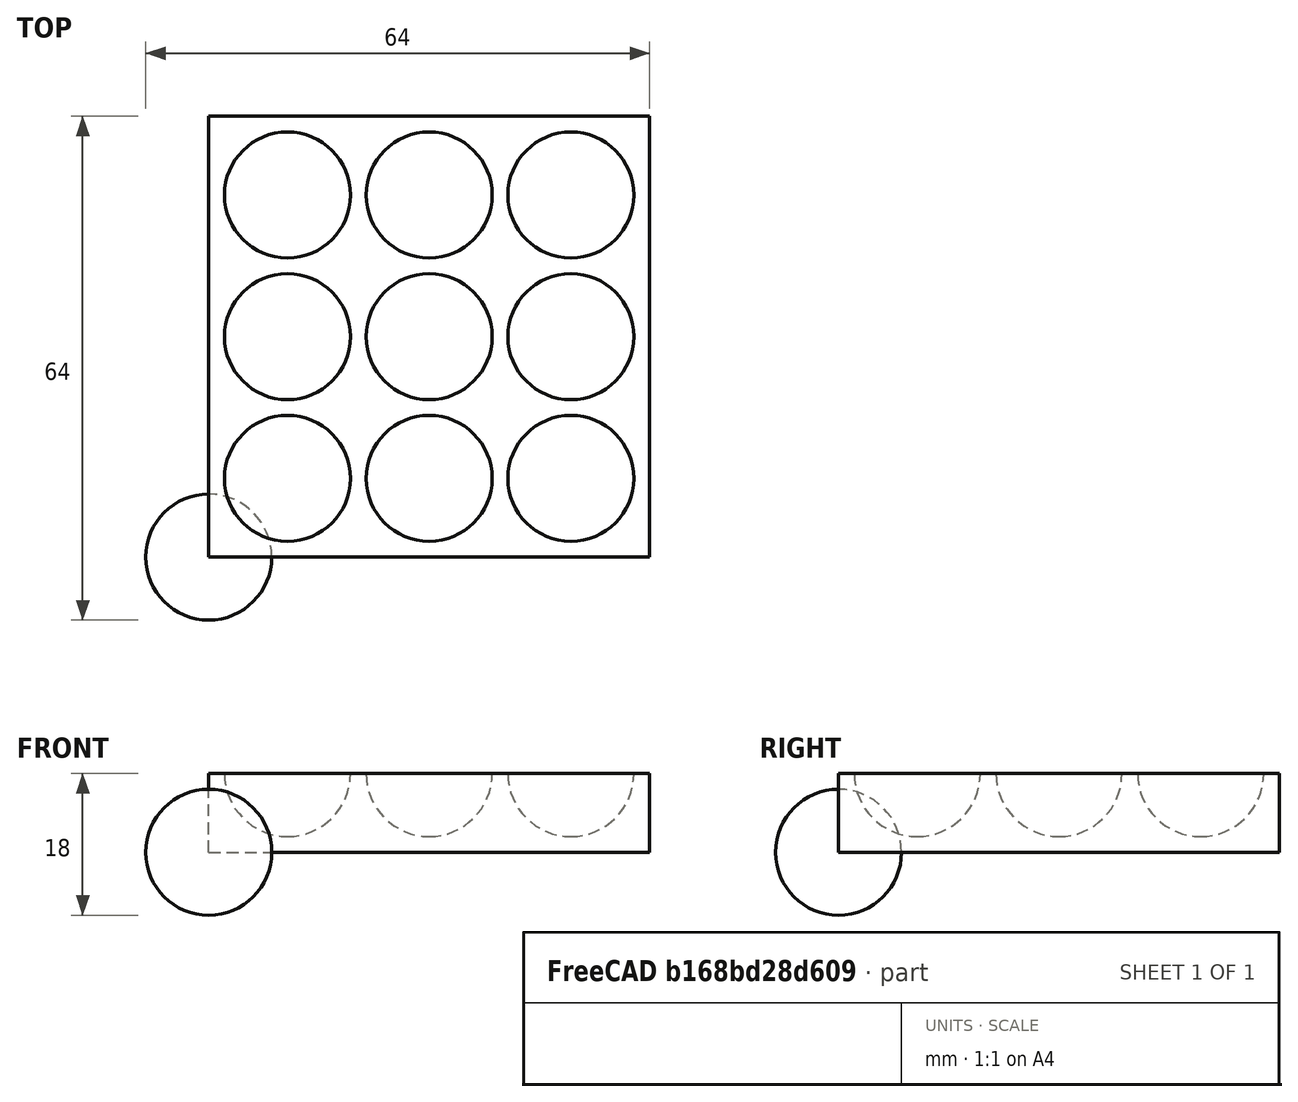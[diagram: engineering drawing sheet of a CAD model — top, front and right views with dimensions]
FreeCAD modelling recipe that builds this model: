
FCSTD DOCUMENT  (FreeCAD 1.0R39319 (Git))
Label: ojt1_t13p01_spheres
License: All rights reserved
LicenseURL: https://en.wikipedia.org/wiki/All_rights_reserved
objects: Part::Sphere×1, Part::FeaturePython×1, Part::Box×1, Part::Cut×1
note: 3 computed .brp shape members not serialized (recipe doc carries the construction recipe); baked Part::Feature solids carry a one-line shape summary decoded from their .brp

FEATURE [Part::Sphere] Sphere  label="Esfera"
  Angle1 = -90
  Angle2 = 90
  Angle3 = 360
  AttacherType = Attacher::AttachEngine3D
  Radius = 8
FEATURE [Part::FeaturePython] Array  # Draft array (typed FeaturePython)
  AlwaysSyncPlacement = false
  Angle = 360
  ArrayType = 0
  Axis = (0,0,1)
  Base = -> Sphere
  Center = (0,0,0)
  Count = 9
  ExpandArray = false
  Fuse = false
  IntervalAxis = (0,0,0)
  IntervalX = (18,0,0)
  IntervalY = (0,18,0)
  IntervalZ = (0,0,100)
  NumberCircles = 3
  NumberPolar = 5
  NumberX = 3
  NumberY = 3
  NumberZ = 1
  Placement = pos=(10,10,10) rot=(0,0,1;0rad)
  PlacementList = 9 placements: [(0,0,0),(0,18,0),(0,36,0),(18,0,0),(18,18,0),(18,36,0),(36,0,0),(36,18,0),(36,36,0)]
  RadialDistance = 50
  ScaleList = (9) [(1,1,1),(1,1,1),(1,1,1),(1,1,1),(1,1,1),(1,1,1),(1,1,1),(1,1,1),(1,1,1)]
  Symmetry = 1
  TangentialDistance = 25
FEATURE [Part::Box] Box  label="Cub"
  AttacherType = Attacher::AttachEngine3D
  Height = 10
  Length = 56
  Width = 56
FEATURE [Part::Cut] Cut
  Base = -> Box
  Tool = -> Array
